# Revit family: xxxxxxxBasin-Topmount-DXV-Modulus-D21050036LH_Series
name_source: partatom
category: Plumbing Fixtures
units: mm (PartAtom-declared; Revit-internal decimal feet)

## family parameters
Always vertical = No
Cut with Voids When Loaded = Yes
OmniClass Number = 23.45.05.14.14
OmniClass Title = Sinks/Lavatories
Part Type = Normal
Room Calculation Point = No
Round Connector Dimension = Use Diameter
Shared = Yes
Work Plane-Based = Yes

## types (2) — shared parameters
Assembly Code = D2010310
Basin Shape = Rectangular
Bowl Depth = 3 3/4"
Bowl Length = 15 3/8"
Bowl Width = 15"
CW Connection = Yes
CWFU = 1.5
Cold Water Connection Diameter = 1/2"
Compliance Certifications = Meets or Exceeds CSA B45.8 / IAPMO Z403
Default Elevation = 34"
Finish = Concrete-DXV-Smoke-409
Grid Drain = No
HW Connection = Yes
HWFU = 1.5
Height = 5 1/16"
Hot Water Connection Diameter = 1/2"
Installation Instruction Link = https://dxv01.blob.core.windows.net
Installation Type = Overcounter
Length = 21"
Manufacturer = DXV
Material = Concrete-DXV-Smoke-409
Price = Prices may vary. Please consult Manufacturer Rep for most up-to-date price list.
Product Documentation Link = https://dxv01.blob.core.windows.net
Product Page URL = https://www.dxv.com
Revised Date = 04/17/2022
URL = https://www.dxv.com
Vent Connection = No
WFU = 2
Waste Connection = Yes
Waste Connection Diameter = 1 1/4"
Width = 36"

## per-type parameters (varying)
| type | Description | Three-Hole |
| D21050036LH.409 | DXV Modulus 36-inch Concrete Bathroom Sink | 6" |
| D21050036LH08.409 | DXV Modulus 36-inch Three-Hole Concrete Bathroom Sink | 3" |

note: column(s) folded — value = type name in every type: Model

type visibility flags (boolean, named after types; folded from table):
- D21050036LH.409: Yes: D21050036LH.409 No-Hole Lavatory
- D21050036LH08.409: Yes: D21050036LH08.409 Three-Hole Lavatory

## geometry (parser evidence)
native form markers: Sweep x2
no freeform markers — native parametric forms only
